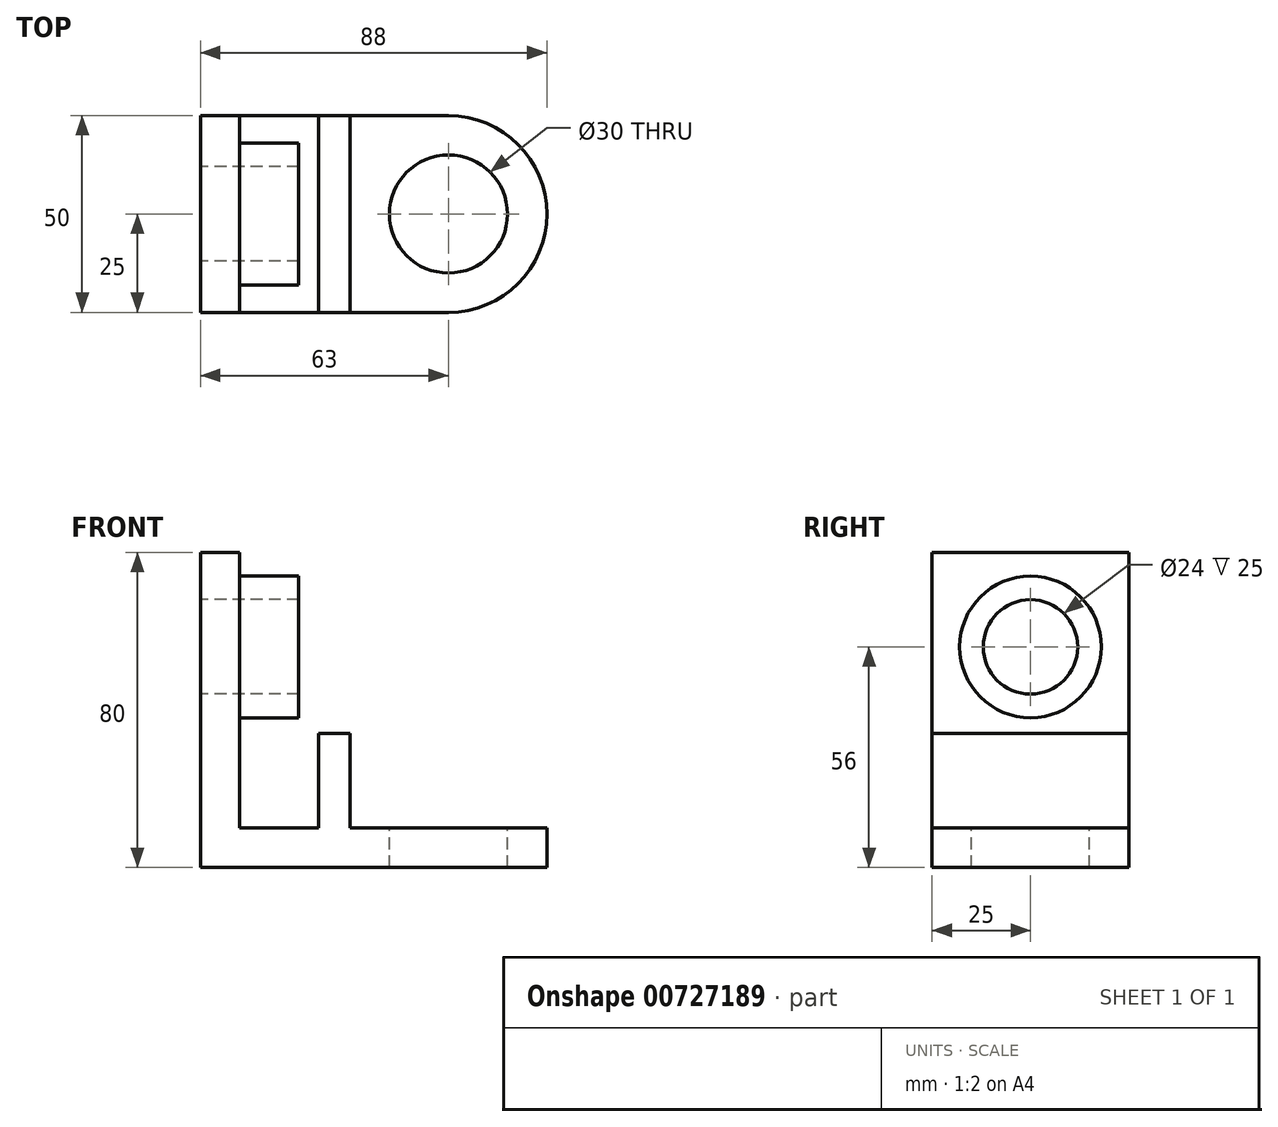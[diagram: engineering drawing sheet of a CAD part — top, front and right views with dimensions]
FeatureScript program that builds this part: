
annotation { "Feature Type Name" : "Feature", "Feature Type Description" : "" }
export const myFeature = defineFeature(function(context is Context, id is Id, definition is map)
    precondition{}
    {
        {
            var Q0;
            Q0=qCreatedBy(makeId("Front.planeOp"),FACE);
            var sketch = newSketch(context, id + "F0", { "sketchPlane" : qUnion([Q0])});
            skLineSegment(sketch, "E0", {"start": v(0, 0) * mm, "end": v(0, 80) * mm});
            skLineSegment(sketch, "E1", {"start": v(0, 80) * mm, "end": v(10, 80) * mm});
            skLineSegment(sketch, "E2", {"start": v(10, 80) * mm, "end": v(10, 10) * mm});
            skLineSegment(sketch, "E3", {"start": v(10, 10) * mm, "end": v(30, 10) * mm});
            skLineSegment(sketch, "E4", {"start": v(30, 10) * mm, "end": v(30, 34) * mm});
            skLineSegment(sketch, "E5", {"start": v(30, 34) * mm, "end": v(38, 34) * mm});
            skLineSegment(sketch, "E6", {"start": v(38, 34) * mm, "end": v(38, 10) * mm});
            skPoint(sketch, "E7.start.orphan", {"position": v(63, 0) * mm});
            skLineSegment(sketch, "E8", {"start": v(38, 10) * mm, "end": v(88, 10) * mm});
            skLineSegment(sketch, "E9", {"start": v(88, 10) * mm, "end": v(88, 0) * mm});
            skLineSegment(sketch, "E10", {"start": v(88, 0) * mm, "end": v(0, 0) * mm});
            skSolve(sketch);
        }
        {
            var Q0;
            Q0 = qSketchRegion(id + "F0", true);
            extrude(context, id + "F1", {"entities" : qUnion([Q0]), "depth" : 50 * mm, "offsetDistance" : 25 * mm});
        }
        {
            var Q0;
            Q0=makeQuery(id+"F1.opExtrude","CAP_EDGE",EDGE,{"disambiguationData":[OSD([sQuery(id+"F0.wireOp",EDGE,"E9")])],"isStart":false});
            var Q1;
            Q1=makeQuery(id+"F1.opExtrude","CAP_EDGE",EDGE,{"disambiguationData":[OSD([sQuery(id+"F0.wireOp",EDGE,"E9")])],"isStart":true});
            fillet(context, id + "F2", {"entities" : qUnion([Q0, Q1]), "radius" : 25 * mm, "tangentPropagation" : true, "allowEdgeOverflow" : false});
        }
        {
            var Q0;
            Q0=makeQuery(id+"F1.opExtrude","SWEPT_FACE",FACE,{"disambiguationData":[OSD([sQuery(id+"F0.wireOp",EDGE,"E8")])]});
            var sketch = newSketch(context, id + "F3", { "sketchPlane" : qUnion([Q0])});
            skCircle(sketch, "E11", {"center": v(63, -25) * mm, "radius": 15 * mm});
            skSolve(sketch);
        }
        {
            var Q0;
            Q0 = qSketchRegion(id + "F3", true);
            extrude(context, id + "F4", {"entities" : qUnion([Q0]), "operationType" : NewBodyOperationType.REMOVE, "endBound" : BoundingType.UP_TO_NEXT, "oppositeDirection" : true, "depth" : 25 * mm, "offsetDistance" : 25 * mm});
        }
        {
            var Q0;
            Q0=makeQuery(id+"F1.opExtrude","SWEPT_FACE",FACE,{"disambiguationData":[OSD([sQuery(id+"F0.wireOp",EDGE,"E2")])]});
            var sketch = newSketch(context, id + "F5", { "sketchPlane" : qUnion([Q0])});
            skCircle(sketch, "E12", {"center": v(-25, 56) * mm, "radius": 18 * mm});
            skCircle(sketch, "E13", {"center": v(-25, 56) * mm, "radius": 12 * mm});
            skSolve(sketch);
        }
        {
            var Q0;
            Q0 = qSketchRegion(id + "F5", true);
            extrude(context, id + "F6", {"entities" : qUnion([Q0]), "operationType" : NewBodyOperationType.ADD, "depth" : 15 * mm, "offsetDistance" : 25 * mm});
        }
        {
            var Q0;
            Q0=makeQuery(id+"F6.boolean.opBoolean","SPLIT",FACE,{"disambiguationData":[TD([makeQuery(id+"F6.opExtrude","SWEPT_FACE",FACE,{"disambiguationData":[OSD([sQuery(id+"F5.wireOp",EDGE,"E13")])]})])],"derivedFrom":makeQuery(id+"F1.opExtrude","SWEPT_FACE",FACE,{"disambiguationData":[OSD([sQuery(id+"F0.wireOp",EDGE,"E2")])]})});
            extrude(context, id + "F7", {"entities" : qUnion([Q0]), "operationType" : NewBodyOperationType.REMOVE, "endBound" : BoundingType.UP_TO_NEXT, "oppositeDirection" : true, "depth" : 25 * mm, "offsetDistance" : 25 * mm});
        }
    });
